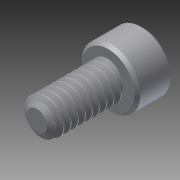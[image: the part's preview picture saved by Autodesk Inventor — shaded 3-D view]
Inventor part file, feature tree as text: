
AUTODESK INVENTOR PART (.ipt)
format: ipt  version: 2015 (Build 190159000, 159)  size: 534,016 bytes
history: native  units: in
note: dims shown in document units (in); Inventor stores cm internally (conversion verified against a paired STEP export)
features: chamfer x1, other x1, imported_body x1
ambient origin geometry x8: Origin, YZ Plane, XZ Plane, XY Plane, X Axis, Y Axis, Z Axis, Center Point
bodies: Body1 (feature_tree)
feature tree (3):
  chamfer  "Chamfer1"  [1 undecoded]
  other  "92185A1321"
  imported_body  "Base1"
note: 1 required parameter value undecoded (feature->parameter linkage not recoverable at this tier; creation-order binding heuristic only, values carry confidence <= 0.55)
